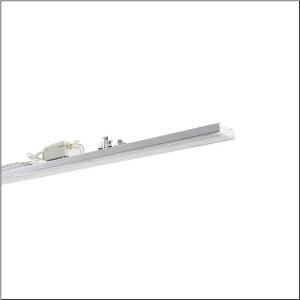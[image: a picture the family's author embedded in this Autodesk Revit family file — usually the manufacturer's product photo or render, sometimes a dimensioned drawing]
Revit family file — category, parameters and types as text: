
# Revit family: licross_r__21_recessed_mo_52tl1edn455g_4166
name_source: partatom
category: Lighting Fixtures
units: mm (PartAtom-declared; Revit-internal decimal feet)

## family parameters
Cut with Voids When Loaded = No
Host = Face
Light Source = No
Part Type = Normal
Room Calculation Point = No
Round Connector Dimension = Use Diameter
Shared = No

## types (1)
- --- (1 x LED, 5800 lm, 32.4 W, 4000K)
    Apparent Load = 32 VA
    CIE Flux Codes = 85 95 99 100 100
    Color Rendering = 80
    Color Temperature = 4000K
    Default Elevation = 1800 mm
    Description = Licross® 21 Recessed MO, luminaire insert, of sheet steel, galvanised, coil coated, white, length: 1.500mm, width: 66mm, height: 67mm, LED rated luminous flux: 5.800lm, light colour: 840, control gear: DALI 2, with plug, 5-pole, with phase selection, mains connection: 220..240V, AC, 50/60Hz, rated input power: 32W, halogen-free wiring, primary light control with lens, of plastic, primary optical cover: cover, of PMMA, light emission: direct distribution, primary light characteristic: symmetric, protection rating (complete): IP40, insulation class (complete): insulation class I (protective earthing), certification: CE, ENEC, VDE, UKCA, protection symbol: D if used in an environment without relevant dust loads with corresponding accessories, impact resistance: IK06, permissible ambient temperature for indoor applications: -25..+45°C, corresponds to IFS (International Featured Standards) requirements for safety and quality in the food industry, reducing of maximum allowable ambient temperature of 5°C with ceiling mounting, LABS conformity tested according to VDMA 24364:2018-05, packaging unit: 1 piece
    Height = 58 mm
    Lamp = 1 x LED
    Lamp Light Flux = 5800 lm
    Lamp Power = 32.4 W
    Lamp count = 1
    Length = 1500 mm
    Luminous efficacy = 179 lm/W
    Manufacturer = Siteco
    ModVariant = No
    Model = 52TL1EDN455G
    Mounting Place = Ceiling
    Mounting Type = Pendant
    Number of Poles = 1
    OnlyDefault = Yes
    Power Factor = 1
    Product Name = Licross® 21 Recessed MO
    Product group = luminaire insert
    ProductGroupID = 901
    Protection Class = Protection class I
    Protection Degree = IP 40
    RLX_Detail_Level = 1
    RLX_Emergency_Light_Flux = 0 lm
    RLX_Emergency_Type = 0
    RLX_Emergency_Type_DB = No
    RlxData = <blob elided: 24325 chars, md5=a9e385ef>
    Socket = socket
    Standby Power = 0 W
    System Light Flux = 5800 lm
    System Power = 32 W
    Type Comments = factory setting: luminous flux: 100 % | dim-lin: 254 | 219 mA
    Type Image = l_1296930.jpg
    URL = http://relux.com
    VarID = @adj_056839
    Voltage = 0 V
    Weight = 0.00 kg
    Width = 66 mm

## geometry (parser evidence)
native form markers: Blend x4, Sweep x10
no freeform markers — native parametric forms only
